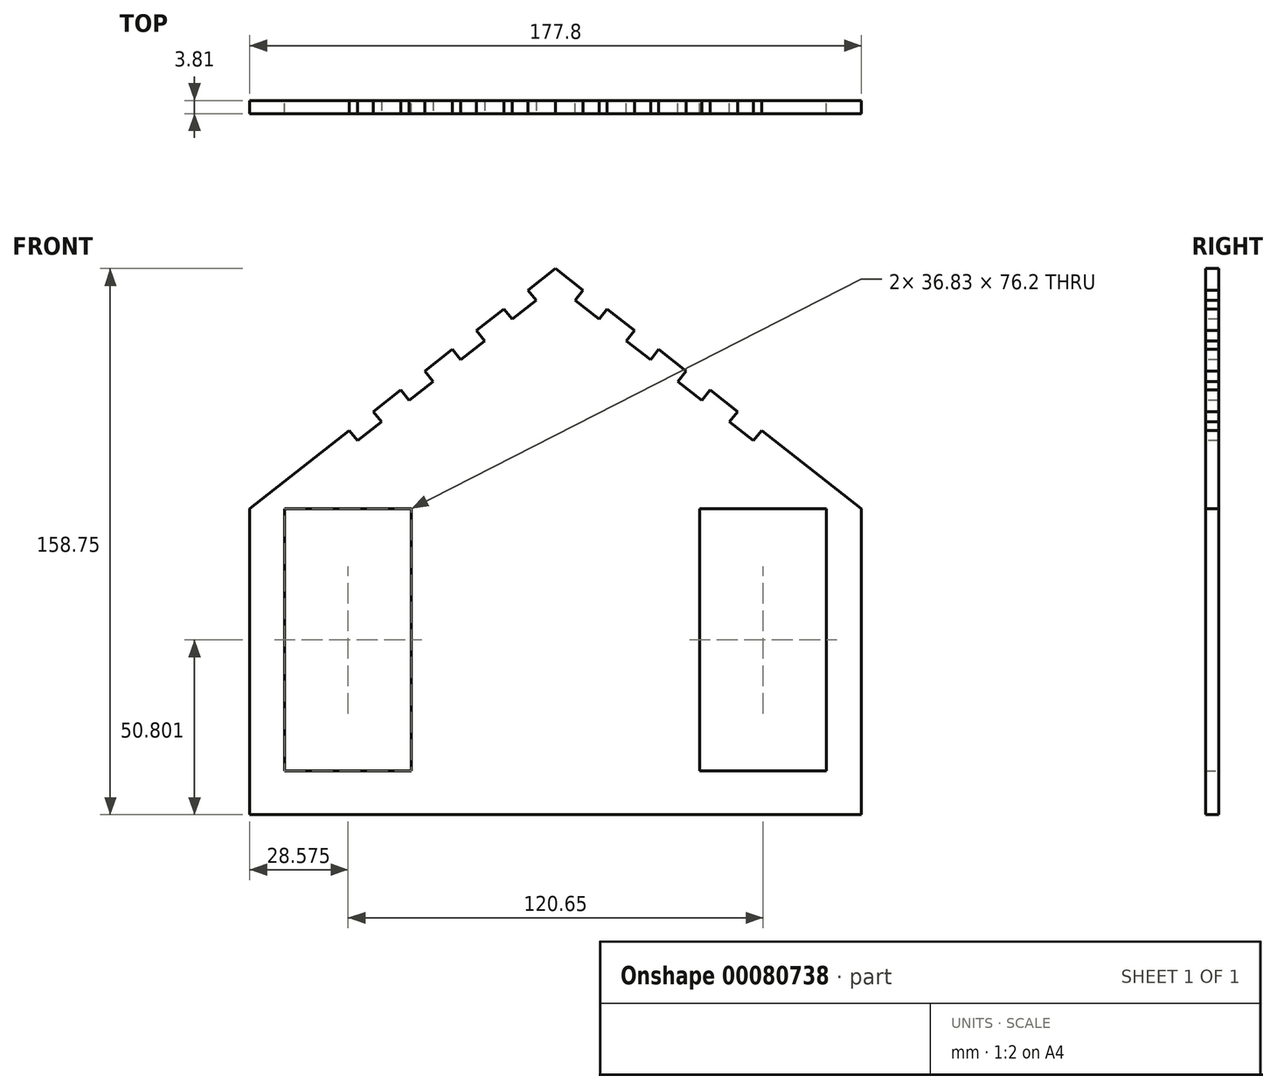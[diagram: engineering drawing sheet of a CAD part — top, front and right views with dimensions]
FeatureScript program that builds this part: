
annotation { "Feature Type Name" : "Feature", "Feature Type Description" : "" }
export const myFeature = defineFeature(function(context is Context, id is Id, definition is map)
    precondition{}
    {
        {
            var Q0;
            Q0=qCreatedBy(makeId("Front.planeOp"),FACE);
            var sketch = newSketch(context, id + "F0", { "sketchPlane" : qUnion([Q0])});
            skLineSegment(sketch, "E0", {"start": v(0, 92.74) * mm, "end": v(0, -66) * mm, "construction": true});
            skLineSegment(sketch, "E1", {"start": v(0, -66) * mm, "end": v(-88.9, -66) * mm});
            skLineSegment(sketch, "E2.MirrorCS", {"start": v(0, -66) * mm, "end": v(88.9, -66) * mm});
            skLineSegment(sketch, "E3", {"start": v(-88.9, -66) * mm, "end": v(-88.9, 22.9) * mm});
            skLineSegment(sketch, "E4", {"start": v(-88.9, 22.9) * mm, "end": v(0, 92.74) * mm});
            skLineSegment(sketch, "E5.MirrorCS", {"start": v(88.9, -66) * mm, "end": v(88.9, 22.9) * mm});
            skLineSegment(sketch, "E6.MirrorCS", {"start": v(88.9, 22.9) * mm, "end": v(0, 92.74) * mm});
            skLineSegment(sketch, "E7.bottom", {"start": v(-78.74, 22.9) * mm, "end": v(-41.91, 22.9) * mm});
            skLineSegment(sketch, "E7.top", {"start": v(-78.74, -53.3) * mm, "end": v(-41.9, -53.3) * mm});
            skLineSegment(sketch, "E7.left", {"start": v(-78.74, 22.9) * mm, "end": v(-78.74, -53.3) * mm});
            skLineSegment(sketch, "E7.right", {"start": v(-41.9, 22.9) * mm, "end": v(-41.9, -53.3) * mm});
            skPoint(sketch, "E7.middle", {"position": v(-60.32, -15.2) * mm});
            skLineSegment(sketch, "E8.MirrorCS", {"start": v(41.91, 22.9) * mm, "end": v(41.91, -53.3) * mm});
            skLineSegment(sketch, "E9.MirrorCS", {"start": v(78.74, 22.9) * mm, "end": v(41.91, 22.9) * mm});
            skLineSegment(sketch, "E10.MirrorCS", {"start": v(78.74, 22.9) * mm, "end": v(78.74, -53.3) * mm});
            skLineSegment(sketch, "E11.MirrorCS", {"start": v(78.74, -53.3) * mm, "end": v(41.91, -53.3) * mm});
            skSolve(sketch);
        }
        {
            var Q0;
            Q0=makeQuery(id+"F0.imprint","IMPRINT",FACE,{"disambiguationData":[TD([[makeQuery(id+"F0.imprint","IMPRINT",EDGE,{"derivedFrom":sQuery(id+"F0.wireOp",EDGE,"E1")}),-1.0]])]});
            extrude(context, id + "F1", {"entities" : qUnion([Q0]), "depth" : 3.8 * mm});
        }
        {
            var Q0;
            Q0=makeQuery(id+"F1.opExtrude","SWEPT_FACE",FACE,{"disambiguationData":[OSD([sQuery(id+"F0.wireOp",EDGE,"E4")])]});
            var sketch = newSketch(context, id + "F2", { "sketchPlane" : qUnion([Q0])});
            skLineSegment(sketch, "E12.bottom", {"start": v(-18.9, 0) * mm, "end": v(-10.01, 0) * mm});
            skLineSegment(sketch, "E12.top", {"start": v(-18.9, -3.81) * mm, "end": v(-10.01, -3.81) * mm});
            skLineSegment(sketch, "E12.left", {"start": v(-18.9, 0) * mm, "end": v(-18.9, -3.81) * mm});
            skLineSegment(sketch, "E12.right", {"start": v(-10.01, 0) * mm, "end": v(-10.01, -3.81) * mm});
            skLineSegment(sketch, "E13.bottom", {"start": v(0.15, 0) * mm, "end": v(9.04, 0) * mm});
            skLineSegment(sketch, "E13.top", {"start": v(0.15, -3.81) * mm, "end": v(9.04, -3.81) * mm});
            skLineSegment(sketch, "E13.left", {"start": v(0.15, 0) * mm, "end": v(0.15, -3.81) * mm});
            skLineSegment(sketch, "E13.right", {"start": v(9.04, 0) * mm, "end": v(9.04, -3.81) * mm});
            skLineSegment(sketch, "E14.bottom", {"start": v(19.2, 0) * mm, "end": v(28.09, 0) * mm});
            skLineSegment(sketch, "E14.top", {"start": v(19.2, -3.81) * mm, "end": v(28.09, -3.81) * mm});
            skLineSegment(sketch, "E14.left", {"start": v(19.2, 0) * mm, "end": v(19.2, -3.81) * mm});
            skLineSegment(sketch, "E14.right", {"start": v(28.09, 0) * mm, "end": v(28.09, -3.81) * mm});
            skLineSegment(sketch, "E15.bottom", {"start": v(38.25, 0) * mm, "end": v(47.14, 0) * mm});
            skLineSegment(sketch, "E15.top", {"start": v(38.25, -3.81) * mm, "end": v(47.14, -3.81) * mm});
            skLineSegment(sketch, "E15.left", {"start": v(38.25, 0) * mm, "end": v(38.25, -3.81) * mm});
            skLineSegment(sketch, "E15.right", {"start": v(47.14, 0) * mm, "end": v(47.14, -3.81) * mm});
            skSolve(sketch);
        }
        {
            var Q0;
            Q0=makeQuery(id+"F2.imprint","IMPRINT",FACE,{"disambiguationData":[TD([[makeQuery(id+"F2.imprint","IMPRINT",EDGE,{"derivedFrom":sQuery(id+"F2.wireOp",EDGE,"E12.bottom")}),-1.0]])]});
            var Q1;
            Q1=makeQuery(id+"F2.imprint","IMPRINT",FACE,{"disambiguationData":[TD([[makeQuery(id+"F2.imprint","IMPRINT",EDGE,{"derivedFrom":sQuery(id+"F2.wireOp",EDGE,"E14.bottom")}),-1.0]])]});
            var Q2;
            Q2=makeQuery(id+"F2.imprint","IMPRINT",FACE,{"disambiguationData":[TD([[makeQuery(id+"F2.imprint","IMPRINT",EDGE,{"derivedFrom":sQuery(id+"F2.wireOp",EDGE,"E15.bottom")}),-1.0]])]});
            var Q3;
            Q3=makeQuery(id+"F2.imprint","IMPRINT",FACE,{"disambiguationData":[TD([[makeQuery(id+"F2.imprint","IMPRINT",EDGE,{"derivedFrom":sQuery(id+"F2.wireOp",EDGE,"E13.bottom")}),-1.0]])]});
            extrude(context, id + "F3", {"entities" : qUnion([Q0, Q1, Q2, Q3]), "operationType" : NewBodyOperationType.REMOVE, "oppositeDirection" : true, "depth" : 3.8 * mm});
        }
        {
            var Q0;
            Q0=makeQuery(id+"F1.opExtrude","SWEPT_FACE",FACE,{"disambiguationData":[OSD([sQuery(id+"F0.wireOp",EDGE,"E6.MirrorCS")])]});
            var sketch = newSketch(context, id + "F4", { "sketchPlane" : qUnion([Q0])});
            skLineSegment(sketch, "E16.bottom", {"start": v(-47.14, -3.81) * mm, "end": v(-38.25, -3.81) * mm});
            skLineSegment(sketch, "E16.top", {"start": v(-47.14, 0) * mm, "end": v(-38.25, 0) * mm});
            skLineSegment(sketch, "E16.left", {"start": v(-47.14, -3.81) * mm, "end": v(-47.14, 0) * mm});
            skLineSegment(sketch, "E16.right", {"start": v(-38.25, -3.8) * mm, "end": v(-38.25, 0) * mm});
            skLineSegment(sketch, "E17.bottom", {"start": v(-28.09, -3.81) * mm, "end": v(-19.2, -3.81) * mm});
            skLineSegment(sketch, "E17.top", {"start": v(-28.09, 0) * mm, "end": v(-19.2, 0) * mm});
            skLineSegment(sketch, "E17.left", {"start": v(-28.09, -3.81) * mm, "end": v(-28.09, 0) * mm});
            skLineSegment(sketch, "E17.right", {"start": v(-19.2, -3.81) * mm, "end": v(-19.2, 0) * mm});
            skLineSegment(sketch, "E18.bottom", {"start": v(-9.04, -3.81) * mm, "end": v(-0.15, -3.81) * mm});
            skLineSegment(sketch, "E18.top", {"start": v(-9.04, 0) * mm, "end": v(-0.15, 0) * mm});
            skLineSegment(sketch, "E18.left", {"start": v(-9.04, -3.81) * mm, "end": v(-9.04, 0) * mm});
            skLineSegment(sketch, "E18.right", {"start": v(-0.15, -3.81) * mm, "end": v(-0.15, 0) * mm});
            skLineSegment(sketch, "E19.bottom", {"start": v(10.01, -3.81) * mm, "end": v(18.9, -3.81) * mm});
            skLineSegment(sketch, "E19.top", {"start": v(10.01, 0) * mm, "end": v(18.9, 0) * mm});
            skLineSegment(sketch, "E19.left", {"start": v(10.01, -3.81) * mm, "end": v(10.01, 0) * mm});
            skLineSegment(sketch, "E19.right", {"start": v(18.9, -3.81) * mm, "end": v(18.9, 0) * mm});
            skSolve(sketch);
        }
        {
            var Q0;
            Q0=makeQuery(id+"F4.imprint","IMPRINT",FACE,{"disambiguationData":[TD([[makeQuery(id+"F4.imprint","IMPRINT",EDGE,{"derivedFrom":sQuery(id+"F4.wireOp",EDGE,"E16.bottom")}),-1.0]])]});
            var Q1;
            Q1=makeQuery(id+"F4.imprint","IMPRINT",FACE,{"disambiguationData":[TD([[makeQuery(id+"F4.imprint","IMPRINT",EDGE,{"derivedFrom":sQuery(id+"F4.wireOp",EDGE,"E17.bottom")}),-1.0]])]});
            var Q2;
            Q2=makeQuery(id+"F4.imprint","IMPRINT",FACE,{"disambiguationData":[TD([[makeQuery(id+"F4.imprint","IMPRINT",EDGE,{"derivedFrom":sQuery(id+"F4.wireOp",EDGE,"E18.bottom")}),-1.0]])]});
            var Q3;
            Q3=makeQuery(id+"F4.imprint","IMPRINT",FACE,{"disambiguationData":[TD([[makeQuery(id+"F4.imprint","IMPRINT",EDGE,{"derivedFrom":sQuery(id+"F4.wireOp",EDGE,"E19.bottom")}),-1.0]])]});
            extrude(context, id + "F5", {"entities" : qUnion([Q0, Q1, Q2, Q3]), "operationType" : NewBodyOperationType.REMOVE, "oppositeDirection" : true, "depth" : 3.8 * mm});
        }
    });
